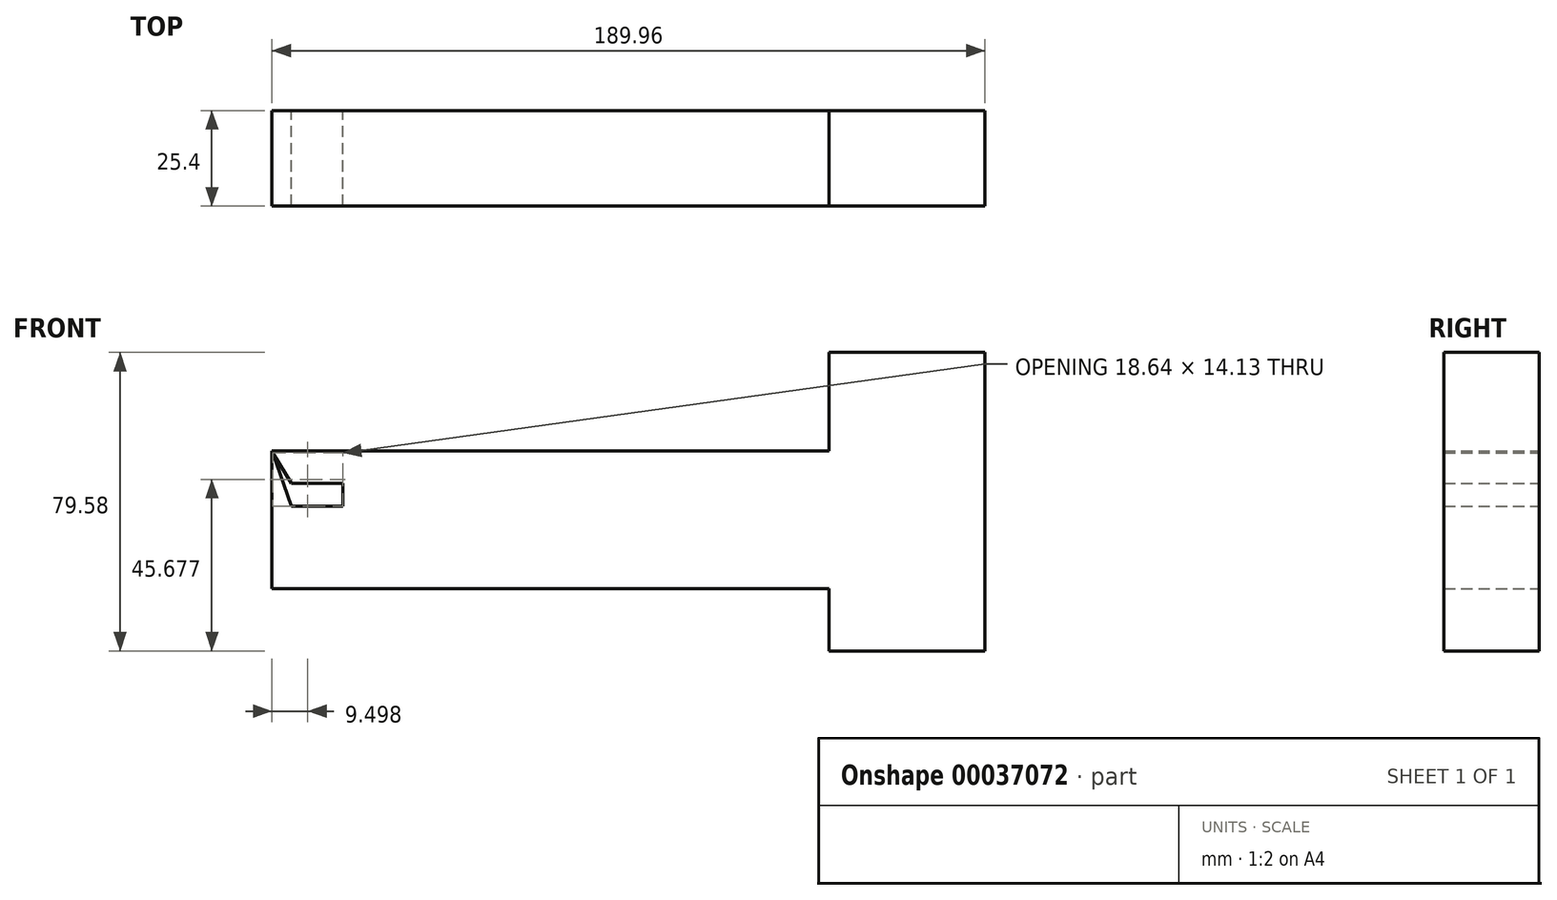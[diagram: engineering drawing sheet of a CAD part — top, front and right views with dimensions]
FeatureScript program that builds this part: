
annotation { "Feature Type Name" : "Feature", "Feature Type Description" : "" }
export const myFeature = defineFeature(function(context is Context, id is Id, definition is map)
    precondition{}
    {
        {
            var Q0;
            Q0=qCreatedBy(makeId("Front.planeOp"),FACE);
            var sketch = newSketch(context, id + "F0", { "sketchPlane" : qUnion([Q0])});
            skLineSegment(sketch, "E0.bottom", {"start": v(-66.31, 40.97) * mm, "end": v(-24.81, 40.97) * mm});
            skLineSegment(sketch, "E0.top", {"start": v(-66.31, -38.6) * mm, "end": v(-24.81, -38.6) * mm});
            skLineSegment(sketch, "E0.left", {"start": v(-66.31, 40.97) * mm, "end": v(-66.31, -38.6) * mm});
            skLineSegment(sketch, "E0.right", {"start": v(-24.81, 40.97) * mm, "end": v(-24.81, -38.6) * mm});
            skLineSegment(sketch, "E1.bottom", {"start": v(-58.19, 14.65) * mm, "end": v(-214.77, 14.65) * mm});
            skLineSegment(sketch, "E1.top", {"start": v(-58.19, -22) * mm, "end": v(-214.77, -22) * mm});
            skLineSegment(sketch, "E1.left", {"start": v(-58.19, 14.65) * mm, "end": v(-58.19, -22) * mm});
            skLineSegment(sketch, "E1.right", {"start": v(-214.77, 14.65) * mm, "end": v(-214.77, -22) * mm});
            skLineSegment(sketch, "E2.bottom", {"start": v(-209.64, 6.01) * mm, "end": v(-195.95, 6.01) * mm});
            skLineSegment(sketch, "E2.top", {"start": v(-209.64, 0) * mm, "end": v(-195.95, 0) * mm});
            skLineSegment(sketch, "E2.left", {"start": v(-209.64, 6.01) * mm, "end": v(-209.64, 0) * mm});
            skLineSegment(sketch, "E2.right", {"start": v(-195.95, 6.01) * mm, "end": v(-195.95, 0) * mm});
            skLineSegment(sketch, "E3", {"start": v(-195.95, 0) * mm, "end": v(-171.56, -22) * mm});
            skLineSegment(sketch, "E4", {"start": v(-209.64, 0) * mm, "end": v(-214.77, 14.65) * mm});
            skLineSegment(sketch, "E5", {"start": v(-215.63, 15.83) * mm, "end": v(-209.64, 6.01) * mm});
            skSolve(sketch);
        }
        {
            var Q0;
            Q0 = qSketchRegion(id + "F0", true);
            extrude(context, id + "F1", {"entities" : qUnion([Q0]), "depth" : 25.4 * mm});
        }
    });
